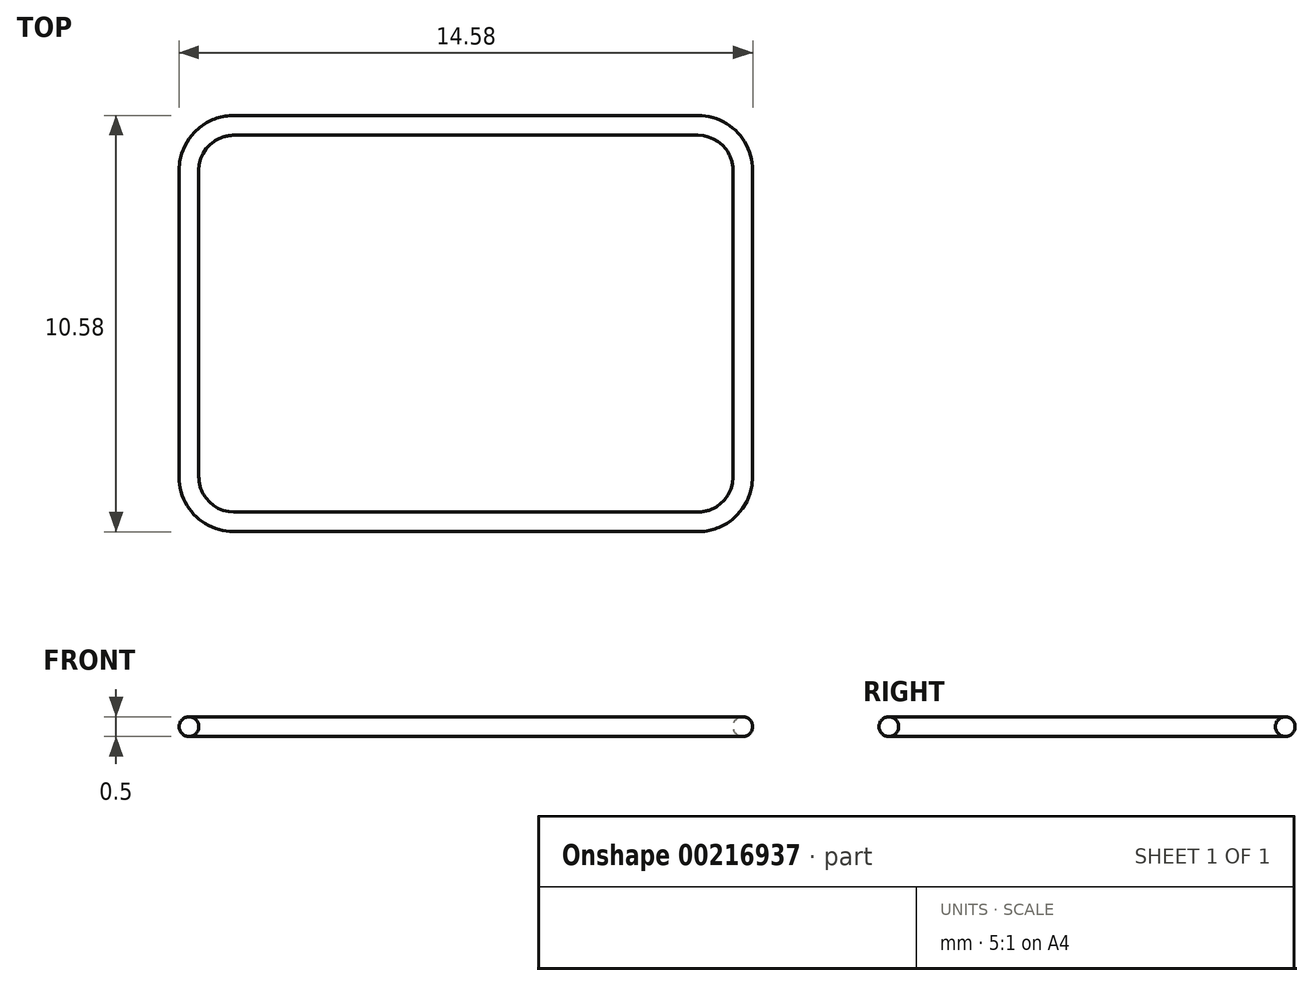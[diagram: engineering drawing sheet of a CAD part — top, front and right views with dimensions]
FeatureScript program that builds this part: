
annotation { "Feature Type Name" : "Feature", "Feature Type Description" : "" }
export const myFeature = defineFeature(function(context is Context, id is Id, definition is map)
    precondition{}
    {
        {
            var Q0;
            Q0=qCreatedBy(makeId("Top.planeOp"),FACE);
            var sketch = newSketch(context, id + "F0", { "sketchPlane" : qUnion([Q0])});
            skLineSegment(sketch, "E0.bottom", {"start": v(5.9, 5.04) * mm, "end": v(-5.9, 5.04) * mm});
            skLineSegment(sketch, "E0.top", {"start": v(5.9, -5.04) * mm, "end": v(-5.9, -5.04) * mm});
            skLineSegment(sketch, "E0.left", {"start": v(7.04, 3.9) * mm, "end": v(7.04, -3.9) * mm});
            skLineSegment(sketch, "E0.right", {"start": v(-7.04, 3.9) * mm, "end": v(-7.04, -3.9) * mm});
            skPoint(sketch, "E0.middle", {"position": v(0, 0) * mm});
            skPoint(sketch, "E1.visualSharp", {"position": v(-7.04, 5.04) * mm});
            skArc(sketch, "E1.filletArc", {"start": v(-5.9, 5.04) * mm, "mid": v(-6.7, 4.7) * mm, "end": v(-7.04, 3.9) * mm});
            skPoint(sketch, "E2.visualSharp", {"position": v(7.04, 5.04) * mm});
            skArc(sketch, "E2.filletArc", {"start": v(7.04, 3.9) * mm, "mid": v(6.7, 4.7) * mm, "end": v(5.9, 5.03) * mm});
            skPoint(sketch, "E3.visualSharp", {"position": v(7.04, -5.04) * mm});
            skArc(sketch, "E3.filletArc", {"start": v(5.9, -5.04) * mm, "mid": v(6.7, -4.7) * mm, "end": v(7.04, -3.9) * mm});
            skPoint(sketch, "E4.visualSharp", {"position": v(-7.04, -5.04) * mm});
            skArc(sketch, "E4.filletArc", {"start": v(-7.04, -3.9) * mm, "mid": v(-6.7, -4.7) * mm, "end": v(-5.9, -5.04) * mm});
            skSolve(sketch);
        }
        {
            var Q0;
            Q0=qCreatedBy(makeId("Front.planeOp"),FACE);
            var Q1;
            Q1=sQuery(id+"F0.wireOp",VERTEX,"E4.filletArc.start");
            cPlane(context, id + "F1", {"entities" : qUnion([Q0, Q1]), "cplaneType" : CPlaneType.PLANE_POINT, "offset" : 25 * mm, "width" : 150 * mm, "height" : 150 * mm});
        }
        {
            var Q0;
            Q0=qCreatedBy(id+"F1.planeOp",FACE);
            var sketch = newSketch(context, id + "F2", { "sketchPlane" : qUnion([Q0])});
            skCircle(sketch, "E5", {"center": v(-7.04, 0) * mm, "radius": 0.25 * mm});
            skSolve(sketch);
        }
        {
            var Q0;
            Q0 = qSketchRegion(id + "F2", true);
            var Q1;
            Q1 = qConstructionFilter(qBodyType(qCreatedBy(id + "F0" ,EDGE), BodyType.WIRE), ConstructionObject.NO);
            sweep(context, id + "F3", {"profiles" : qUnion([Q0]), "path" : qUnion([Q1])});
        }
    });
